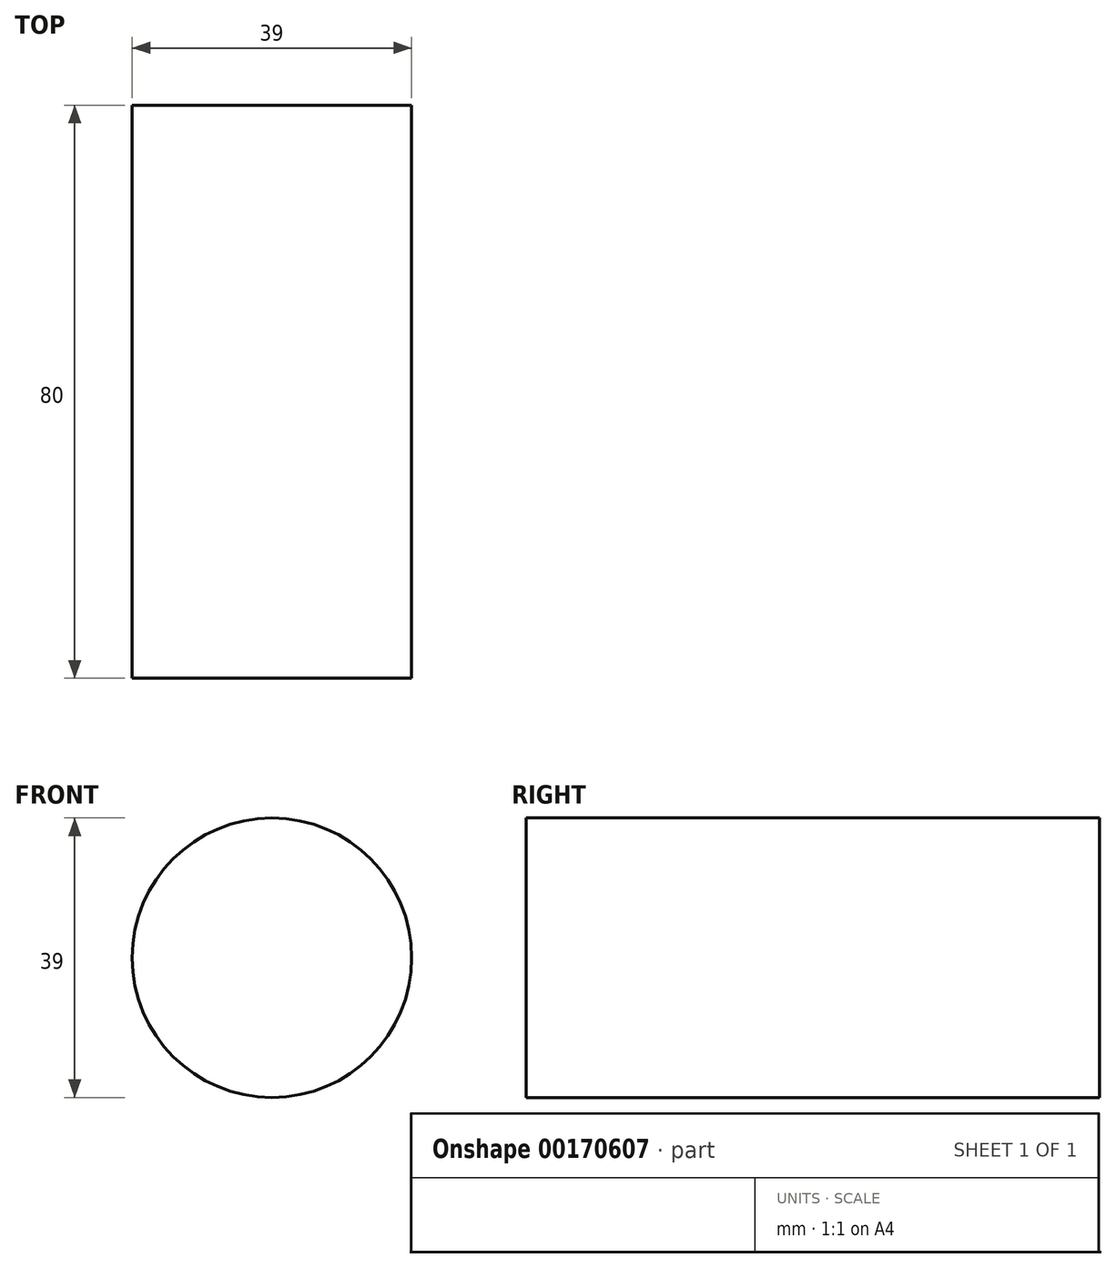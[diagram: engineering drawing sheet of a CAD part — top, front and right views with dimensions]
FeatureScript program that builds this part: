
annotation { "Feature Type Name" : "Feature", "Feature Type Description" : "" }
export const myFeature = defineFeature(function(context is Context, id is Id, definition is map)
    precondition{}
    {
        {
            var Q0;
            Q0=qCreatedBy(makeId("Front.planeOp"),FACE);
            var sketch = newSketch(context, id + "F0", { "sketchPlane" : qUnion([Q0])});
            skCircle(sketch, "E0", {"center": v(0, 0) * mm, "radius": 19.5 * mm});
            skSolve(sketch);
        }
        {
            var Q0;
            Q0=makeQuery(id+"F0.imprint","IMPRINT",FACE,{"disambiguationData":[TD([[makeQuery(id+"F0.imprint","IMPRINT",EDGE,{"derivedFrom":sQuery(id+"F0.wireOp",EDGE,"E0")}),1.0]])]});
            extrude(context, id + "F1", {"entities" : qUnion([Q0]), "depth" : 80 * mm});
        }
    });
